# Revit family: FantiniCosmi_BIM_CH180WIFI LITE
name_source: partatom
category: Generic Models
units: mm (PartAtom-declared; Revit-internal decimal feet)

## family parameters
Always vertical = Yes
Can host rebar = No
Cut with Voids When Loaded = No
Part Type = Normal
Room Calculation Point = No
Round Connector Dimension = Use Diameter
Shared = No
Work Plane-Based = No

## types (1)
- Standard
    Adjustable antifreeze temperature range = 2 ÷ 7 °C
    Catalog web link = https://www.fantinicosmi.it
    Default Elevation = 0 mm  [stored 0 ft]
    Description = Cronotermostato settimanale touchscreen, a batterie
    Differential = 0.3 ÷ 5 K
    Displayed temperature = -35 ÷ 50 °C
    Electric insulation  = Double insulation
    Part Number = Intellicomfort CH180WIFILITE
    Power supply = 230V-50Hz
    Protection degree = IP40
    Pulse voltage = 4000V
    Software = A class
    Temperature range = 2 ÷ 40 °C
    Thermal gradient = 4K/h.
    Type of action = 1BU (connection micro-switch)
    WiFi connection = 2.4 GHz (802.11 b/g/n)

note: [stored X ft] marks values corroborated as IEEE doubles in the binary element streams (Revit-internal decimal feet)

## geometry (parser evidence)
native form markers: Sweep x2
no freeform markers — native parametric forms only
